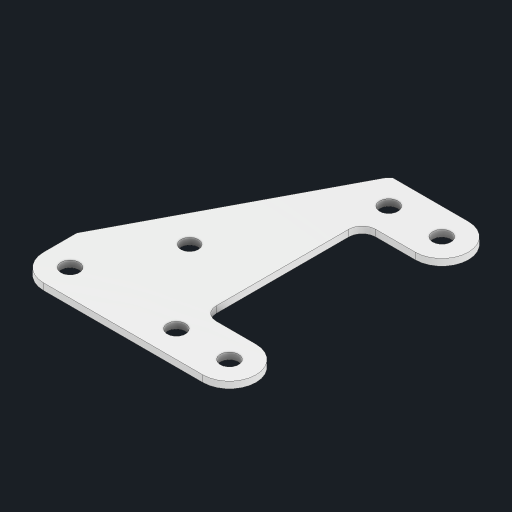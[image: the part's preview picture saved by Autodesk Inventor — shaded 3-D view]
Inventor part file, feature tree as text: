
AUTODESK INVENTOR PART (.ipt)
format: ipt  version: 2024 (Build 280153000, 153)  size: 125,440 bytes
history: native  units: in
note: dims shown in document units (in); Inventor stores cm internally (conversion verified against a paired STEP export)
features: other x3, extrude x1, sketch x1
ambient origin geometry x8: Origin, YZ Plane, XZ Plane, XY Plane, X Axis, Y Axis, Z Axis, Center Point
bodies: Solid1 (feature_tree)
feature tree (5):
  other  "Blocks"
  extrude  "Extrusion1"  Depth=0.0625in TaperAngle=0.0deg
  sketch  "Sketch1"  dims[d0=0.125in d1=0.0625in d2=0.0in d3=0.165in]
  other  "main"
  other  "main:1"
